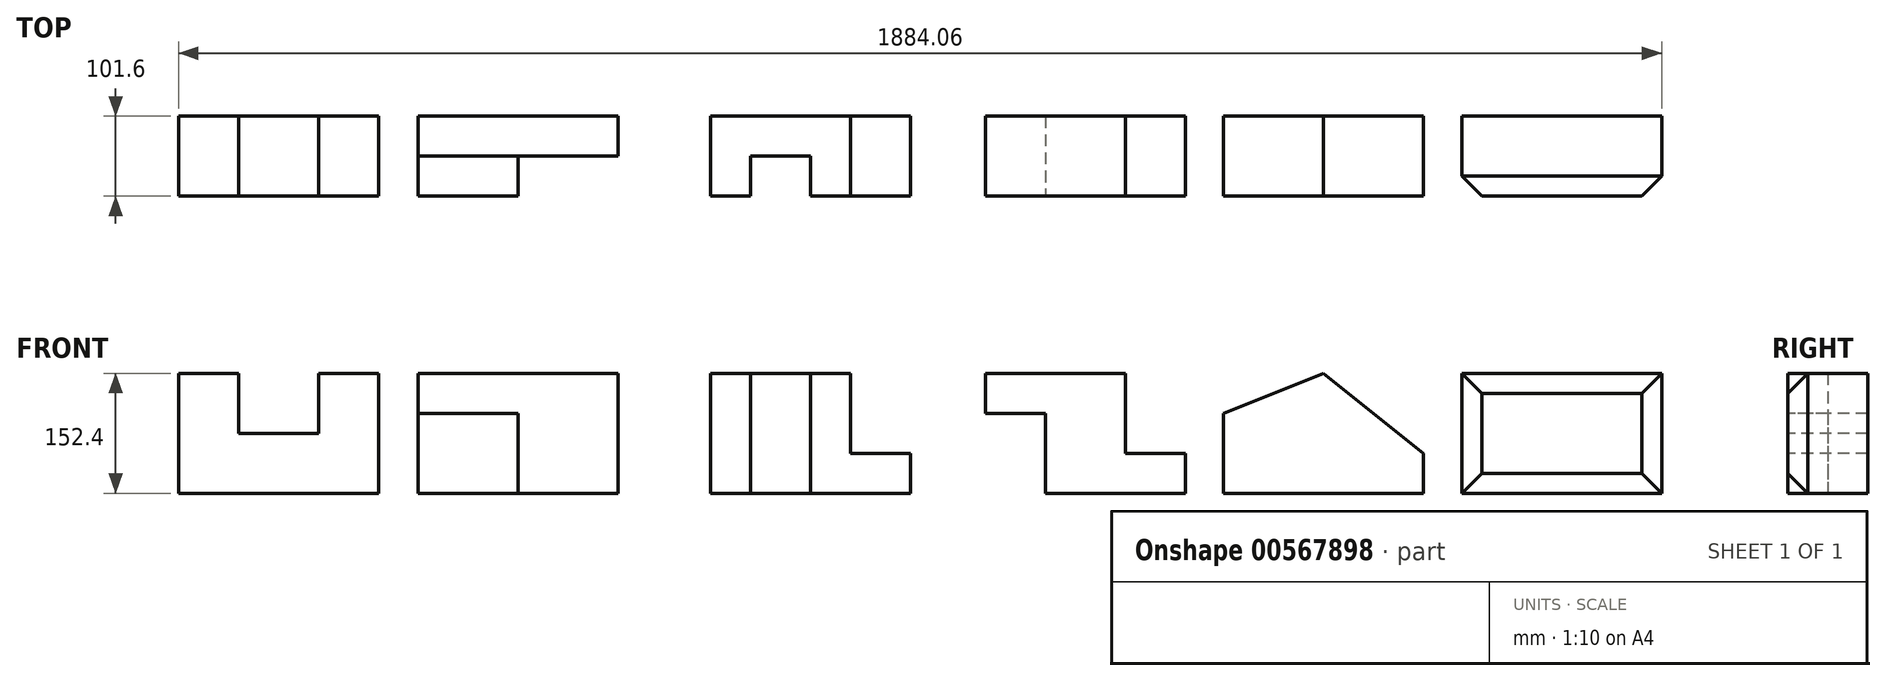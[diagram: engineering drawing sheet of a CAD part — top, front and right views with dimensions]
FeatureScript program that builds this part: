
annotation { "Feature Type Name" : "Feature", "Feature Type Description" : "" }
export const myFeature = defineFeature(function(context is Context, id is Id, definition is map)
    precondition{}
    {
        {
            var Q0;
            Q0=qCreatedBy(makeId("Front.planeOp"),FACE);
            var sketch = newSketch(context, id + "F0", { "sketchPlane" : qUnion([Q0])});
            skLineSegment(sketch, "E0", {"start": v(0, 0) * mm, "end": v(127, 0) * mm});
            skLineSegment(sketch, "E1", {"start": v(0, 0) * mm, "end": v(-127, 0) * mm});
            skLineSegment(sketch, "E2", {"start": v(-127, 0) * mm, "end": v(-127, 152.4) * mm});
            skLineSegment(sketch, "E3", {"start": v(-127, 152.4) * mm, "end": v(-50.8, 152.4) * mm});
            skLineSegment(sketch, "E4", {"start": v(-50.8, 152.4) * mm, "end": v(-50.8, 76.2) * mm});
            skLineSegment(sketch, "E5", {"start": v(-50.8, 76.2) * mm, "end": v(50.8, 76.2) * mm});
            skLineSegment(sketch, "E6", {"start": v(50.8, 76.2) * mm, "end": v(50.8, 152.4) * mm});
            skLineSegment(sketch, "E7", {"start": v(50.8, 152.4) * mm, "end": v(127, 152.4) * mm});
            skLineSegment(sketch, "E8", {"start": v(127, 152.4) * mm, "end": v(127, 0) * mm});
            skSolve(sketch);
        }
        {
            var Q0;
            Q0=makeQuery(id+"F0.imprint","IMPRINT",FACE,{"disambiguationData":[TD([[makeQuery(id+"F0.imprint","IMPRINT",EDGE,{"derivedFrom":sQuery(id+"F0.wireOp",EDGE,"E0")}),1.0]])]});
            extrude(context, id + "F1", {"entities" : qUnion([Q0]), "oppositeDirection" : true, "depth" : 101.6 * mm, "offsetDistance" : 25.4 * mm});
        }
        {
            var Q0;
            Q0=qCreatedBy(makeId("Top.planeOp"),FACE);
            var sketch = newSketch(context, id + "F2", { "sketchPlane" : qUnion([Q0])});
            skLineSegment(sketch, "E9", {"start": v(177.44, 0) * mm, "end": v(177.44, 101.6) * mm});
            skLineSegment(sketch, "E10", {"start": v(177.44, 101.6) * mm, "end": v(431.44, 101.6) * mm});
            skLineSegment(sketch, "E11", {"start": v(431.44, 101.6) * mm, "end": v(431.44, 50.8) * mm});
            skLineSegment(sketch, "E12", {"start": v(431.44, 50.8) * mm, "end": v(304.44, 50.8) * mm});
            skLineSegment(sketch, "E13", {"start": v(304.44, 50.8) * mm, "end": v(304.44, 0) * mm});
            skLineSegment(sketch, "E14", {"start": v(304.44, 0) * mm, "end": v(177.44, 0) * mm});
            skSolve(sketch);
        }
        {
            var Q0;
            Q0=makeQuery(id+"F2.imprint","IMPRINT",FACE,{"disambiguationData":[TD([[makeQuery(id+"F2.imprint","IMPRINT",EDGE,{"derivedFrom":sQuery(id+"F2.wireOp",EDGE,"E9")}),-1.0]])]});
            extrude(context, id + "F3", {"entities" : qUnion([Q0]), "depth" : 152.4 * mm, "offsetDistance" : 25.4 * mm});
        }
        {
            var Q0;
            Q0=makeQuery(id+"F3.opExtrude","SWEPT_FACE",FACE,{"disambiguationData":[OSD([sQuery(id+"F2.wireOp",EDGE,"E14")])]});
            var sketch = newSketch(context, id + "F4", { "sketchPlane" : qUnion([Q0])});
            skLineSegment(sketch, "E15", {"start": v(177.44, 0) * mm, "end": v(177.44, 101.6) * mm});
            skLineSegment(sketch, "E16", {"start": v(177.44, 101.6) * mm, "end": v(304.44, 101.6) * mm});
            skSolve(sketch);
        }
        {
            var Q0;
            Q0 = qSketchRegion(id + "F4", true);
            var Q1;
            {var subQ0=sQuery(id+"F4.wireOp",EDGE,"E16");Q1=makeQuery(id+"F4.imprint","IMPRINT",FACE,{"disambiguationData":[TD([[makeQuery(id+"F4.imprint","IMPRINT",EDGE,{"derivedFrom":subQ0}),1.0]])]});}
            extrude(context, id + "F5", {"entities" : qUnion([Q0, Q1]), "operationType" : NewBodyOperationType.REMOVE, "oppositeDirection" : true, "depth" : 50.8 * mm, "offsetDistance" : 25.4 * mm});
        }
        {
            var Q0;
            Q0=qCreatedBy(makeId("Front.planeOp"),FACE);
            var sketch = newSketch(context, id + "F6", { "sketchPlane" : qUnion([Q0])});
            skLineSegment(sketch, "E17", {"start": v(432.98, 0) * mm, "end": v(497.97, 0) * mm});
            skLineSegment(sketch, "E18", {"start": v(497.97, 0) * mm, "end": v(548.77, 0) * mm});
            skLineSegment(sketch, "E19", {"start": v(548.77, 0) * mm, "end": v(548.77, 152.4) * mm});
            skLineSegment(sketch, "E20", {"start": v(548.77, 152.4) * mm, "end": v(599.57, 152.4) * mm});
            skLineSegment(sketch, "E21", {"start": v(599.57, 152.4) * mm, "end": v(599.57, 0) * mm});
            skLineSegment(sketch, "E22", {"start": v(599.57, 0) * mm, "end": v(548.77, 0) * mm});
            skLineSegment(sketch, "E23", {"start": v(599.57, 152.4) * mm, "end": v(726.57, 152.4) * mm});
            skLineSegment(sketch, "E24", {"start": v(726.57, 152.4) * mm, "end": v(726.57, 50.8) * mm});
            skLineSegment(sketch, "E25", {"start": v(726.57, 50.8) * mm, "end": v(802.77, 50.8) * mm});
            skLineSegment(sketch, "E26", {"start": v(802.77, 50.8) * mm, "end": v(802.77, 0) * mm});
            skLineSegment(sketch, "E27", {"start": v(802.77, 0) * mm, "end": v(599.57, 0) * mm});
            skSolve(sketch);
        }
        {
            var Q0;
            Q0 = qSketchRegion(id + "F6", true);
            extrude(context, id + "F7", {"entities" : qUnion([Q0]), "oppositeDirection" : true, "depth" : 101.6 * mm, "offsetDistance" : 25.4 * mm});
        }
        {
            var Q0;
            Q0=makeQuery(id+"F7.opExtrude","CAP_FACE",FACE,{"disambiguationData":[OSD([sQuery(id+"F6.wireOp",EDGE,"E19"),sQuery(id+"F6.wireOp",EDGE,"E20"),sQuery(id+"F6.wireOp",EDGE,"E22"),sQuery(id+"F6.wireOp",EDGE,"E23"),sQuery(id+"F6.wireOp",EDGE,"E24"),sQuery(id+"F6.wireOp",EDGE,"E25"),sQuery(id+"F6.wireOp",EDGE,"E26"),sQuery(id+"F6.wireOp",EDGE,"E27")])],"isStart":true});
            var sketch = newSketch(context, id + "F8", { "sketchPlane" : qUnion([Q0])});
            skLineSegment(sketch, "E28", {"start": v(548.77, 0) * mm, "end": v(599.57, 0) * mm});
            skLineSegment(sketch, "E29", {"start": v(599.57, 0) * mm, "end": v(599.57, 152.4) * mm});
            skLineSegment(sketch, "E30", {"start": v(599.57, 152.4) * mm, "end": v(675.77, 152.4) * mm});
            skLineSegment(sketch, "E31", {"start": v(675.77, 152.4) * mm, "end": v(675.77, 0) * mm});
            skLineSegment(sketch, "E32", {"start": v(675.77, 0) * mm, "end": v(599.57, 0) * mm});
            skSolve(sketch);
        }
        {
            var Q0;
            Q0=makeQuery(id+"F8.imprint","IMPRINT",FACE,{"disambiguationData":[TD([[makeQuery(id+"F8.imprint","IMPRINT",EDGE,{"derivedFrom":sQuery(id+"F8.wireOp",EDGE,"E29")}),-1.0]])]});
            extrude(context, id + "F9", {"entities" : qUnion([Q0]), "operationType" : NewBodyOperationType.REMOVE, "oppositeDirection" : true, "depth" : 50.8 * mm, "offsetDistance" : 25.4 * mm});
        }
        {
            var Q0;
            Q0=qCreatedBy(makeId("Front.planeOp"),FACE);
            var sketch = newSketch(context, id + "F10", { "sketchPlane" : qUnion([Q0])});
            skLineSegment(sketch, "E33", {"start": v(898.26, 152.4) * mm, "end": v(1076.06, 152.4) * mm});
            skLineSegment(sketch, "E34", {"start": v(1076.06, 152.4) * mm, "end": v(1076.06, 50.8) * mm});
            skLineSegment(sketch, "E35", {"start": v(1076.06, 50.8) * mm, "end": v(1152.26, 50.8) * mm});
            skLineSegment(sketch, "E36", {"start": v(1152.26, 50.8) * mm, "end": v(1152.26, 0) * mm});
            skLineSegment(sketch, "E37", {"start": v(1152.26, 0) * mm, "end": v(974.46, 0) * mm});
            skLineSegment(sketch, "E38", {"start": v(974.46, 0) * mm, "end": v(974.46, 101.6) * mm});
            skLineSegment(sketch, "E39", {"start": v(974.46, 101.6) * mm, "end": v(898.26, 101.6) * mm});
            skPoint(sketch, "E39.endSnap0", {"position": v(898.26, 76.2) * mm});
            skLineSegment(sketch, "E40", {"start": v(898.26, 101.6) * mm, "end": v(898.26, 152.4) * mm});
            skSolve(sketch);
        }
        {
            var Q0;
            Q0=makeQuery(id+"F10.imprint","IMPRINT",FACE,{"disambiguationData":[TD([[makeQuery(id+"F10.imprint","IMPRINT",EDGE,{"derivedFrom":sQuery(id+"F10.wireOp",EDGE,"E33")}),-1.0]])]});
            extrude(context, id + "F11", {"entities" : qUnion([Q0]), "oppositeDirection" : true, "depth" : 101.6 * mm, "offsetDistance" : 25.4 * mm});
        }
        {
            var Q0;
            Q0=qCreatedBy(makeId("Front.planeOp"),FACE);
            var sketch = newSketch(context, id + "F12", { "sketchPlane" : qUnion([Q0])});
            skLineSegment(sketch, "E41", {"start": v(1200.18, 0) * mm, "end": v(1200.18, 101.6) * mm});
            skLineSegment(sketch, "E42", {"start": v(1200.18, 0) * mm, "end": v(1454.18, 0) * mm});
            skLineSegment(sketch, "E43", {"start": v(1454.18, 0) * mm, "end": v(1454.18, 50.8) * mm});
            skLineSegment(sketch, "E44", {"start": v(1327.18, 152.4) * mm, "end": v(1200.18, 101.6) * mm});
            skLineSegment(sketch, "E45", {"start": v(1327.18, 152.4) * mm, "end": v(1454.18, 50.8) * mm});
            skSolve(sketch);
        }
        {
            var Q0;
            Q0 = qSketchRegion(id + "F12", true);
            extrude(context, id + "F13", {"entities" : qUnion([Q0]), "oppositeDirection" : true, "depth" : 101.6 * mm, "offsetDistance" : 25.4 * mm});
        }
        {
            var Q0;
            Q0=qCreatedBy(makeId("Front.planeOp"),FACE);
            var sketch = newSketch(context, id + "F14", { "sketchPlane" : qUnion([Q0])});
            skLineSegment(sketch, "E46", {"start": v(1503.06, 0) * mm, "end": v(1757.06, 0) * mm});
            skLineSegment(sketch, "E47", {"start": v(1757.06, 0) * mm, "end": v(1757.06, 152.4) * mm});
            skLineSegment(sketch, "E48", {"start": v(1757.06, 152.4) * mm, "end": v(1503.06, 152.4) * mm});
            skLineSegment(sketch, "E49", {"start": v(1503.06, 152.4) * mm, "end": v(1503.06, 0) * mm});
            skSolve(sketch);
        }
        {
            var Q0;
            Q0 = qSketchRegion(id + "F14", true);
            extrude(context, id + "F15", {"entities" : qUnion([Q0]), "oppositeDirection" : true, "depth" : 101.6 * mm, "offsetDistance" : 25.4 * mm});
        }
        {
            var Q0;
            Q0=makeQuery(id+"F15.opExtrude","CAP_EDGE",EDGE,{"disambiguationData":[OSD([sQuery(id+"F14.wireOp",EDGE,"E48")])],"isStart":true});
            var Q1;
            Q1=makeQuery(id+"F15.opExtrude","CAP_EDGE",EDGE,{"disambiguationData":[OSD([sQuery(id+"F14.wireOp",EDGE,"E47")])],"isStart":true});
            var Q2;
            Q2=makeQuery(id+"F15.opExtrude","CAP_EDGE",EDGE,{"disambiguationData":[OSD([sQuery(id+"F14.wireOp",EDGE,"E46")])],"isStart":true});
            var Q3;
            Q3=makeQuery(id+"F15.opExtrude","CAP_EDGE",EDGE,{"disambiguationData":[OSD([sQuery(id+"F14.wireOp",EDGE,"E49")])],"isStart":true});
            chamfer(context, id + "F16", {"entities" : qUnion([Q0, Q1, Q2, Q3]), "width" : 25.4 * mm, "tangentPropagation" : true});
        }
    });
